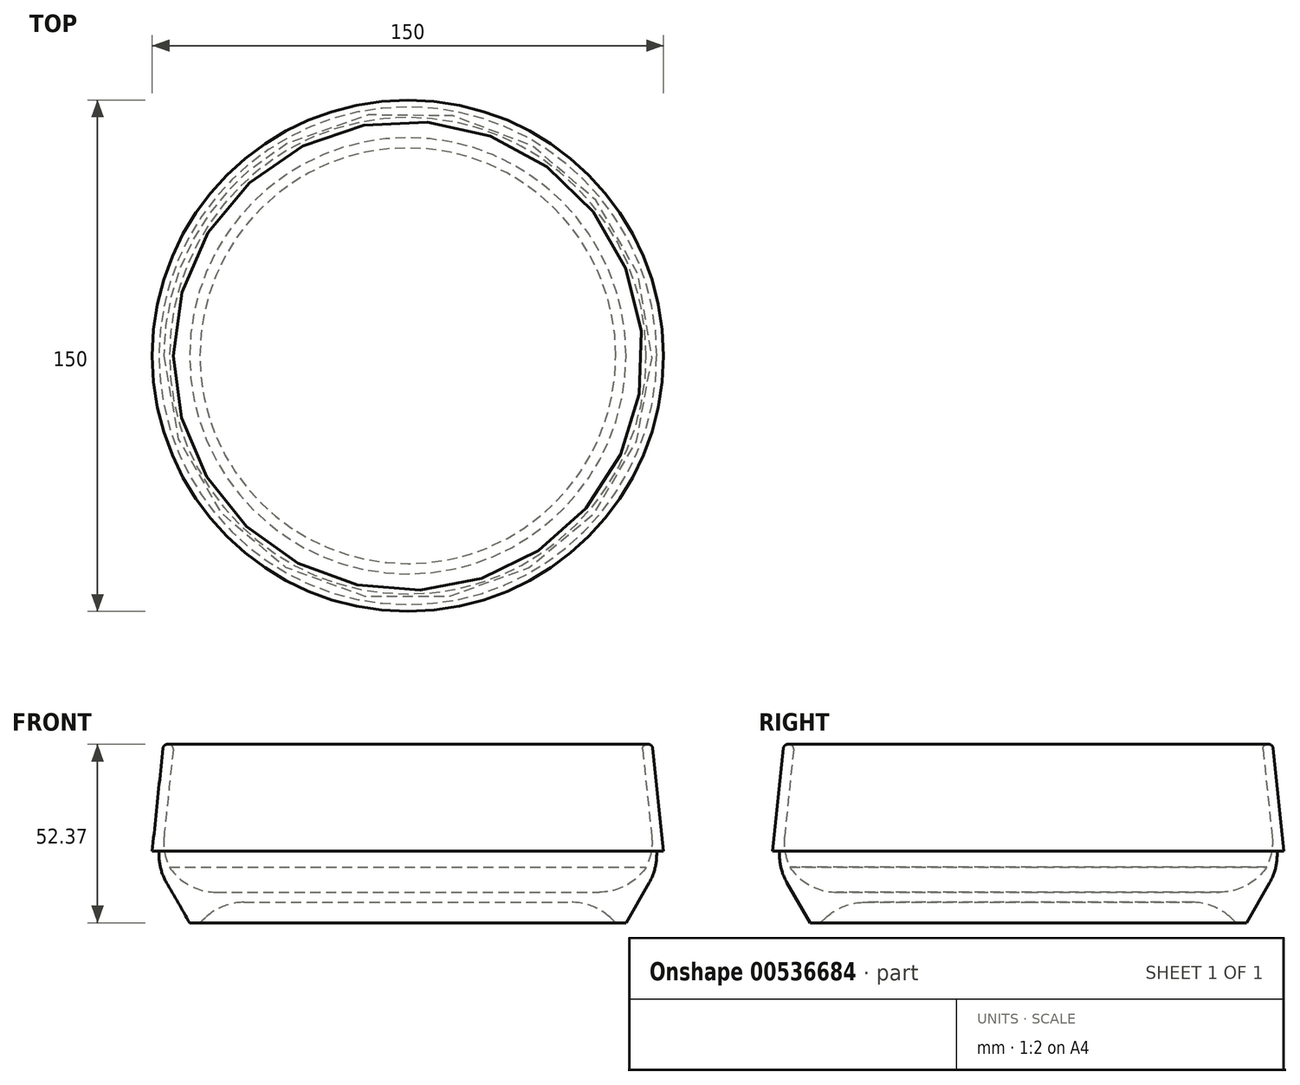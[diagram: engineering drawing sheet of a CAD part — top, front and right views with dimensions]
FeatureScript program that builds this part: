
annotation { "Feature Type Name" : "Feature", "Feature Type Description" : "" }
export const myFeature = defineFeature(function(context is Context, id is Id, definition is map)
    precondition{}
    {
        {
            var Q0;
            Q0=qCreatedBy(makeId("Front.planeOp"),FACE);
            var sketch = newSketch(context, id + "F0", { "sketchPlane" : qUnion([Q0])});
            skLineSegment(sketch, "E0", {"start": v(0, 6) * mm, "end": v(48.08, 6) * mm});
            skLineSegment(sketch, "E1", {"start": v(59.3, 1.6) * mm, "end": v(61, 0) * mm});
            skLineSegment(sketch, "E2", {"start": v(61, 0) * mm, "end": v(64, 0) * mm});
            skLineSegment(sketch, "E3", {"start": v(64, 0) * mm, "end": v(70.8, 11.77) * mm});
            skLineSegment(sketch, "E4", {"start": v(73, 20) * mm, "end": v(73, 21) * mm});
            skLineSegment(sketch, "E5", {"start": v(73, 21) * mm, "end": v(75, 21) * mm});
            skLineSegment(sketch, "E6", {"start": v(75, 21) * mm, "end": v(71.83, 51.2) * mm});
            skLineSegment(sketch, "E7", {"start": v(70.4, 52.36) * mm, "end": v(70, 52.32) * mm});
            skLineSegment(sketch, "E8", {"start": v(68.84, 50.9) * mm, "end": v(71.53, 25.33) * mm});
            skLineSegment(sketch, "E9", {"start": v(70.48, 17.23) * mm, "end": v(69.41, 15.38) * mm});
            skLineSegment(sketch, "E10", {"start": v(56.23, 9) * mm, "end": v(0, 9) * mm});
            skLineSegment(sketch, "E11", {"start": v(0, 9) * mm, "end": v(0, 6) * mm});
            skPoint(sketch, "E12.visualSharp", {"position": v(54.55, 6) * mm});
            skArc(sketch, "E12.filletArc", {"start": v(59.3, 1.6) * mm, "mid": v(54.1, 4.86) * mm, "end": v(48.08, 6) * mm});
            skPoint(sketch, "E13.visualSharp", {"position": v(65.73, 9) * mm});
            skArc(sketch, "E13.filletArc", {"start": v(56.23, 9) * mm, "mid": v(64.46, 11.2) * mm, "end": v(70.48, 17.23) * mm});
            skPoint(sketch, "E14.visualSharp", {"position": v(72.09, 20) * mm});
            skArc(sketch, "E14.filletArc", {"start": v(69.41, 15.38) * mm, "mid": v(71.26, 20.18) * mm, "end": v(71.53, 25.33) * mm});
            skPoint(sketch, "E15.visualSharp", {"position": v(73, 15.59) * mm});
            skArc(sketch, "E15.filletArc", {"start": v(70.8, 11.77) * mm, "mid": v(72.44, 15.74) * mm, "end": v(73, 20) * mm});
            skPoint(sketch, "E16.visualSharp", {"position": v(71.69, 52.5) * mm});
            skArc(sketch, "E16.filletArc", {"start": v(71.83, 51.2) * mm, "mid": v(71.35, 52.08) * mm, "end": v(70.4, 52.36) * mm});
            skPoint(sketch, "E17.visualSharp", {"position": v(68.7, 52.19) * mm});
            skArc(sketch, "E17.filletArc", {"start": v(70, 52.32) * mm, "mid": v(69.12, 51.85) * mm, "end": v(68.84, 50.9) * mm});
            skLineSegment(sketch, "E18", {"start": v(75, 21) * mm, "end": v(75, 52.5) * mm, "construction": true});
            skLineSegment(sketch, "E19", {"start": v(0, 0) * mm, "end": v(0, 51.2) * mm, "construction": true});
            skSolve(sketch);
        }
        {
            var Q0;
            Q0=qSketchRegion(id+"F0",true);
            var Q1;
            Q1=sQuery(id+"F0.wireOp",EDGE,"E19");
            revolve(context, id + "F1", {"entities" : qUnion([Q0]), "axis" : qUnion([Q1]), "revolveType" : RevolveType.FULL});
        }
    });
